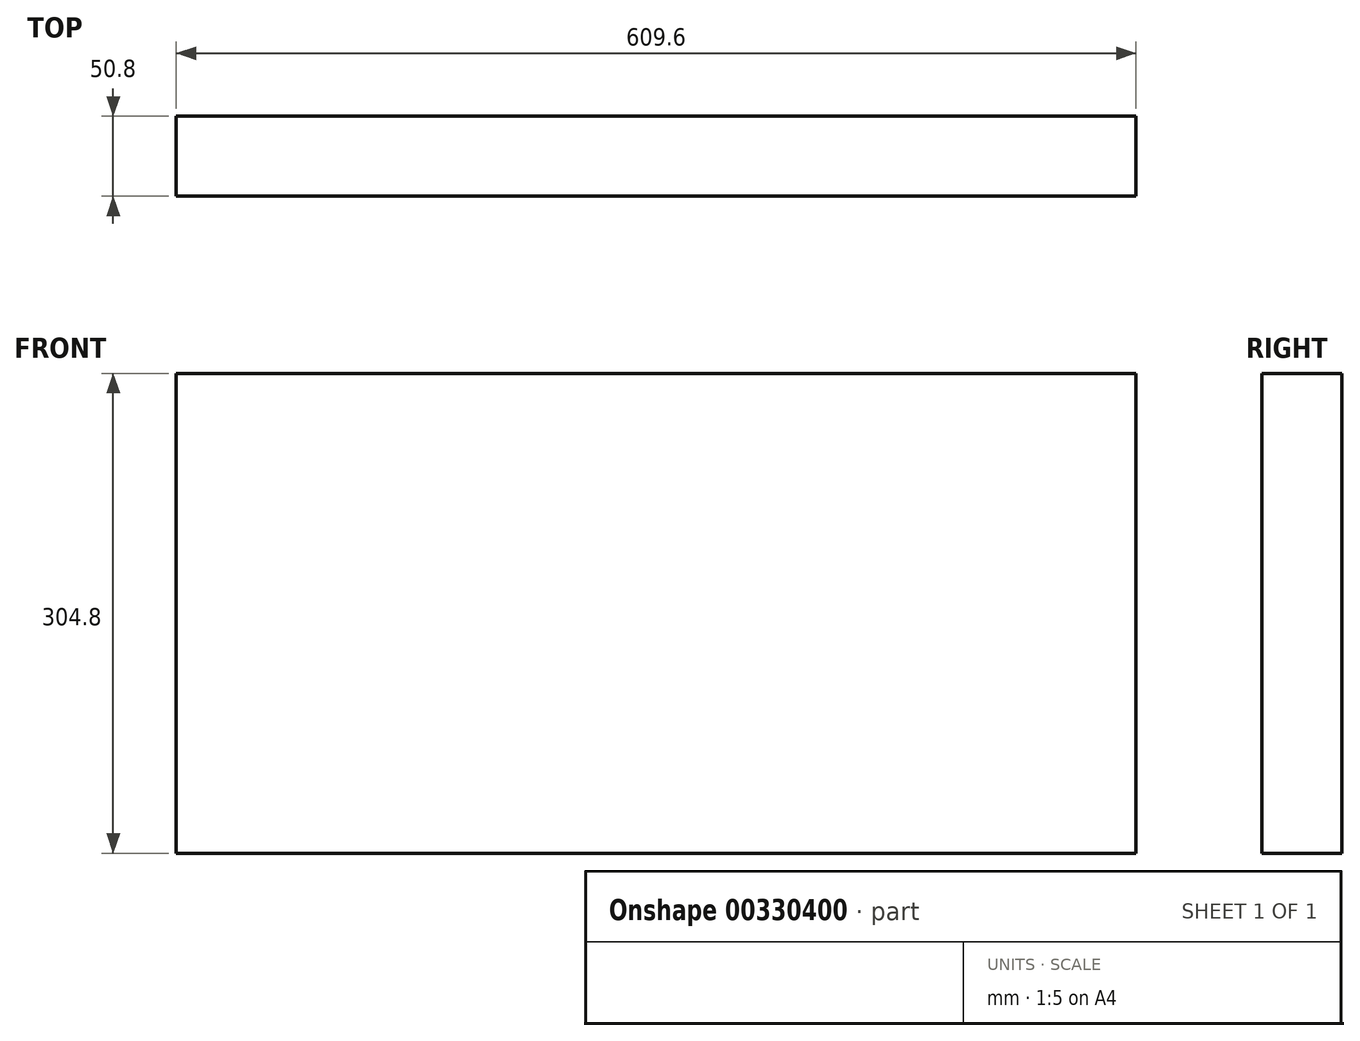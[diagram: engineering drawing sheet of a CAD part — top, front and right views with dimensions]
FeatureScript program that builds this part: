
annotation { "Feature Type Name" : "Feature", "Feature Type Description" : "" }
export const myFeature = defineFeature(function(context is Context, id is Id, definition is map)
    precondition{}
    {
        {
            var Q0;
            Q0=qCreatedBy(makeId("Front.planeOp"),FACE);
            var sketch = newSketch(context, id + "F0", { "sketchPlane" : qUnion([Q0])});
            skLineSegment(sketch, "E0.bottom", {"start": v(-296.17, 93.26) * mm, "end": v(313.43, 93.26) * mm});
            skLineSegment(sketch, "E0.top", {"start": v(-296.17, -211.54) * mm, "end": v(313.43, -211.54) * mm});
            skLineSegment(sketch, "E0.left", {"start": v(-296.17, 93.26) * mm, "end": v(-296.17, -211.54) * mm});
            skLineSegment(sketch, "E0.right", {"start": v(313.43, 93.26) * mm, "end": v(313.43, -211.54) * mm});
            skSolve(sketch);
        }
        {
            var Q0;
            Q0=makeQuery(id+"F0.imprint","IMPRINT",FACE,{"disambiguationData":[TD([[makeQuery(id+"F0.imprint","IMPRINT",EDGE,{"derivedFrom":sQuery(id+"F0.wireOp",EDGE,"E0.bottom")}),-1.0]])]});
            extrude(context, id + "F1", {"entities" : qUnion([Q0]), "depth" : 50.8 * mm});
        }
    });
